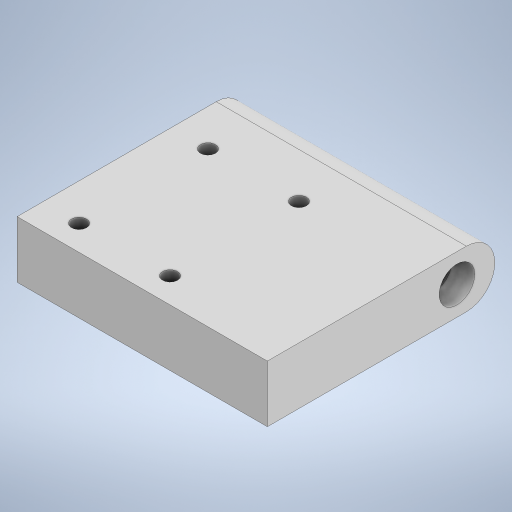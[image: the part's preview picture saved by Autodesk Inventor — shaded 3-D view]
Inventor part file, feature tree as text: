
AUTODESK INVENTOR PART (.ipt)
format: ipt  version: 2024.2 (Build 282272000, 272)  size: 244,736 bytes
history: native  units: in
note: dims shown in document units (in); Inventor stores cm internally (conversion verified against a paired STEP export)
features: extrude x4, sketch x4, other x1
ambient origin geometry x8: Origin, YZ Plane, XZ Plane, XY Plane, X Axis, Y Axis, Z Axis, Center Point
bodies: Solid1 (feature_tree)
feature tree (9):
  extrude  "Extrusion1"  Depth=1.5in
  extrude  "Extrusion2"  Depth=0.375in
  extrude  "Extrusion3"  Depth=0.1875in
  extrude  "Extrusion4"  Depth=0.15in
  other  "Full Round Fillet1"
  sketch  "Sketch1"  dims[d0=1.65in d1=1.5in]
  sketch  "Sketch2"  dims[d2=0.375in d3=0.0in d4=0.118in]
  sketch  "Sketch3"  dims[d5=0.1875in d6=0.25in]
  sketch  "Sketch4"  dims[d7=0.0in d8=0.0in d9=0.235in d10=0.15in d11=0.0in d12=0.85in d14=0.6in d16=0.1in d17=0.1in d18=0.15in d19=0.0in d20=0.1in]
